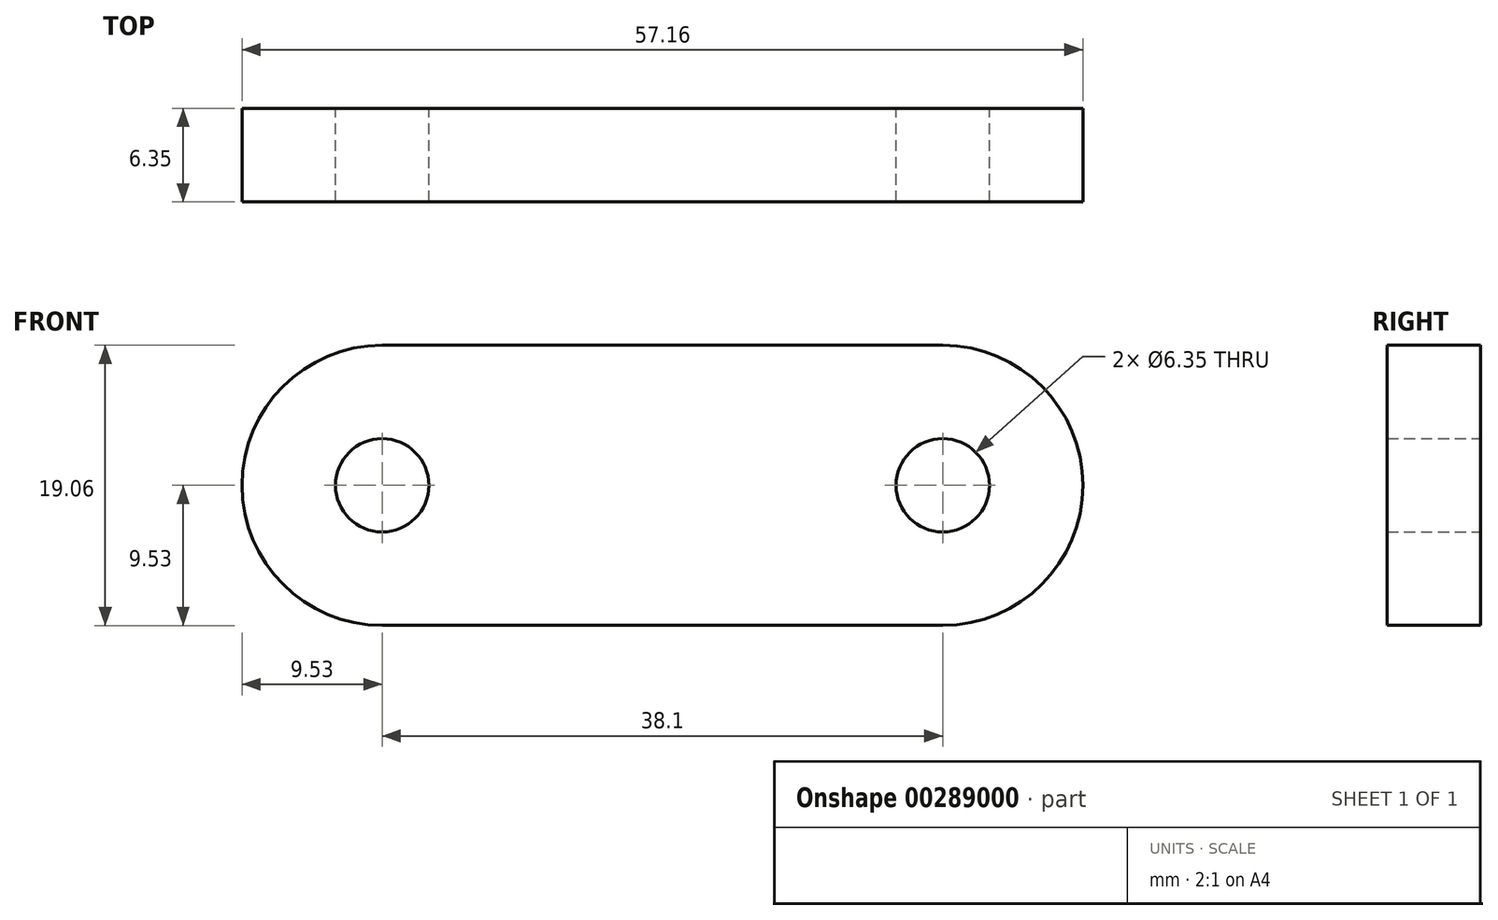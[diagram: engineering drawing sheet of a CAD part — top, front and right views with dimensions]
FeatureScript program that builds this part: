
annotation { "Feature Type Name" : "Feature", "Feature Type Description" : "" }
export const myFeature = defineFeature(function(context is Context, id is Id, definition is map)
    precondition{}
    {
        {
            var Q0;
            Q0=qCreatedBy(makeId("Front.planeOp"),FACE);
            var sketch = newSketch(context, id + "F0", { "sketchPlane" : qUnion([Q0])});
            skLineSegment(sketch, "E0.bottom", {"start": v(-19.05, 9.53) * mm, "end": v(19.05, 9.53) * mm});
            skLineSegment(sketch, "E0.top", {"start": v(-19.05, -9.53) * mm, "end": v(19.05, -9.53) * mm});
            skPoint(sketch, "E0.middle", {"position": v(0, 0) * mm});
            skArc(sketch, "E1", {"start": v(19.05, -9.53) * mm, "mid": v(28.58, 0) * mm, "end": v(19.05, 9.53) * mm});
            skCircle(sketch, "E2", {"center": v(19.05, 0) * mm, "radius": 3.18 * mm});
            skCircle(sketch, "E3", {"center": v(-19.05, 0) * mm, "radius": 3.18 * mm});
            skArc(sketch, "E4", {"start": v(-19.05, 9.53) * mm, "mid": v(-28.58, 0) * mm, "end": v(-19.05, -9.53) * mm});
            skSolve(sketch);
        }
        {
            var Q0;
            Q0=makeQuery(id+"F0.imprint","IMPRINT",FACE,{"disambiguationData":[TD([[makeQuery(id+"F0.imprint","IMPRINT",EDGE,{"derivedFrom":sQuery(id+"F0.wireOp",EDGE,"E0.bottom")}),-1.0]])]});
            extrude(context, id + "F1", {"entities" : qUnion([Q0]), "depth" : 6.35 * mm});
        }
    });
